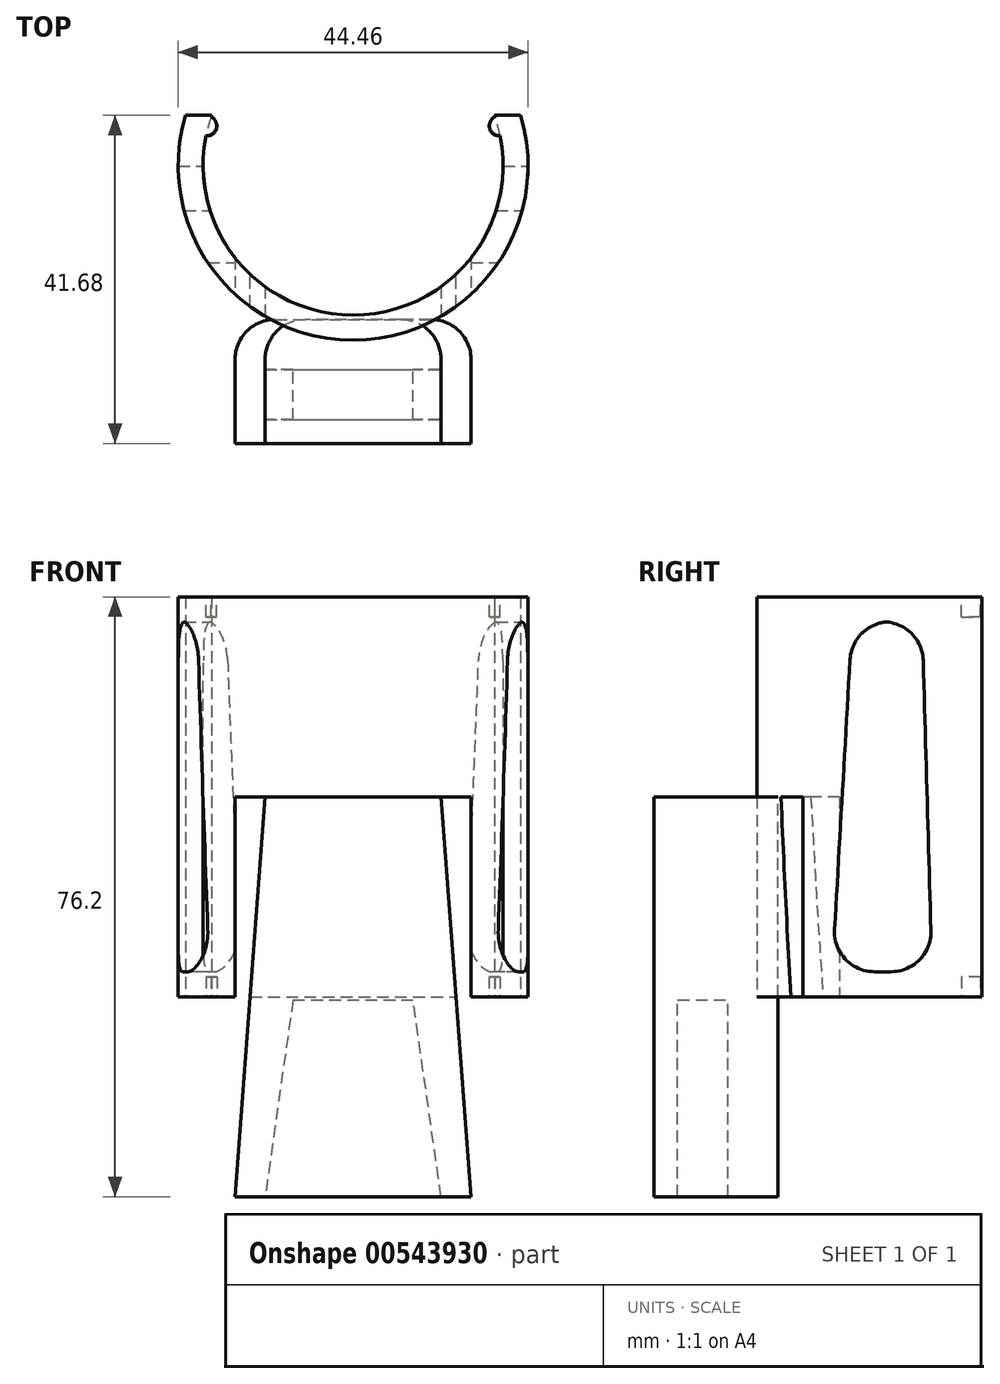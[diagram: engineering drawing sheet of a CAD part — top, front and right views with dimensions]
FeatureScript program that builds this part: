
annotation { "Feature Type Name" : "Feature", "Feature Type Description" : "" }
export const myFeature = defineFeature(function(context is Context, id is Id, definition is map)
    precondition{}
    {
        {
            var Q0;
            Q0=qCreatedBy(makeId("Top.planeOp"),FACE);
            var sketch = newSketch(context, id + "F0", { "sketchPlane" : qUnion([Q0])});
            skArc(sketch, "E0", {"start": v(-17.96, 6.35) * mm, "mid": v(0, -19.05) * mm, "end": v(17.96, 6.35) * mm});
            skArc(sketch, "E1.0", {"start": v(-21.3, 6.35) * mm, "mid": v(0, -22.23) * mm, "end": v(21.3, 6.35) * mm});
            skLineSegment(sketch, "E2", {"start": v(21.3, 6.35) * mm, "end": v(17.96, 6.35) * mm});
            skLineSegment(sketch, "E3.trimOffspring", {"start": v(-17.96, 6.35) * mm, "end": v(-21.3, 6.35) * mm});
            skSolve(sketch);
        }
        {
            var Q0;
            Q0=qSketchRegion(id+"F0",true);
            extrude(context, id + "F1", {"entities" : qUnion([Q0]), "depth" : 50.8 * mm});
        }
        {
            var Q0;
            Q0=qCreatedBy(makeId("Right.planeOp"),FACE);
            var sketch = newSketch(context, id + "F2", { "sketchPlane" : qUnion([Q0])});
            skLineSegment(sketch, "E4", {"start": v(-10.16, 47.63) * mm, "end": v(-1.27, 47.63) * mm});
            skLineSegment(sketch, "E5", {"start": v(-1.27, 47.63) * mm, "end": v(0, 3.18) * mm});
            skLineSegment(sketch, "E6", {"start": v(0, 3.18) * mm, "end": v(-12.7, 3.17) * mm});
            skLineSegment(sketch, "E7", {"start": v(-12.7, 3.18) * mm, "end": v(-10.16, 47.62) * mm});
            skSolve(sketch);
        }
        {
            var Q0;
            Q0=qSketchRegion(id+"F2",true);
            extrude(context, id + "F3", {"entities" : qUnion([Q0]), "operationType" : NewBodyOperationType.REMOVE, "endBound" : BoundingType.SYMMETRIC, "depth" : 78.74 * mm});
        }
        {
            var Q0;
            Q0=makeQuery(id+"F3.boolean.opBoolean","COPY",EDGE,{"disambiguationData":[OD(1.0)],"derivedFrom":makeQuery(id+"F3.opExtrude","SWEPT_EDGE",EDGE,{"disambiguationData":[OSD([sQuery(id+"F2.wireOp",EDGE,"E4"),sQuery(id+"F2.wireOp",EDGE,"E7")])]})});
            var Q1;
            Q1=makeQuery(id+"F3.boolean.opBoolean","COPY",EDGE,{"disambiguationData":[OD(1.0)],"derivedFrom":makeQuery(id+"F3.opExtrude","SWEPT_EDGE",EDGE,{"disambiguationData":[OSD([sQuery(id+"F2.wireOp",EDGE,"E4"),sQuery(id+"F2.wireOp",EDGE,"E5")])]})});
            var Q2;
            Q2=makeQuery(id+"F3.boolean.opBoolean","COPY",EDGE,{"disambiguationData":[OD(1.0)],"derivedFrom":makeQuery(id+"F3.opExtrude","SWEPT_EDGE",EDGE,{"disambiguationData":[OSD([sQuery(id+"F2.wireOp",EDGE,"E5"),sQuery(id+"F2.wireOp",EDGE,"E6")])]})});
            var Q3;
            Q3=makeQuery(id+"F3.boolean.opBoolean","COPY",EDGE,{"disambiguationData":[OD(1.0)],"derivedFrom":makeQuery(id+"F3.opExtrude","SWEPT_EDGE",EDGE,{"disambiguationData":[OSD([sQuery(id+"F2.wireOp",EDGE,"E6"),sQuery(id+"F2.wireOp",EDGE,"E7")])]})});
            var Q4;
            Q4=makeQuery(id+"F3.boolean.opBoolean","COPY",EDGE,{"disambiguationData":[OD(0.0)],"derivedFrom":makeQuery(id+"F3.opExtrude","SWEPT_EDGE",EDGE,{"disambiguationData":[OSD([sQuery(id+"F2.wireOp",EDGE,"E6"),sQuery(id+"F2.wireOp",EDGE,"E7")])]})});
            var Q5;
            Q5=makeQuery(id+"F3.boolean.opBoolean","COPY",EDGE,{"disambiguationData":[OD(0.0)],"derivedFrom":makeQuery(id+"F3.opExtrude","SWEPT_EDGE",EDGE,{"disambiguationData":[OSD([sQuery(id+"F2.wireOp",EDGE,"E5"),sQuery(id+"F2.wireOp",EDGE,"E6")])]})});
            var Q6;
            Q6=makeQuery(id+"F3.boolean.opBoolean","COPY",EDGE,{"disambiguationData":[OD(0.0)],"derivedFrom":makeQuery(id+"F3.opExtrude","SWEPT_EDGE",EDGE,{"disambiguationData":[OSD([sQuery(id+"F2.wireOp",EDGE,"E4"),sQuery(id+"F2.wireOp",EDGE,"E7")])]})});
            var Q7;
            Q7=makeQuery(id+"F3.boolean.opBoolean","COPY",EDGE,{"disambiguationData":[OD(0.0)],"derivedFrom":makeQuery(id+"F3.opExtrude","SWEPT_EDGE",EDGE,{"disambiguationData":[OSD([sQuery(id+"F2.wireOp",EDGE,"E4"),sQuery(id+"F2.wireOp",EDGE,"E5")])]})});
            fillet(context, id + "F4", {"entities" : qUnion([Q0, Q1, Q2, Q3, Q4, Q5, Q6, Q7]), "radius" : 5.08 * mm, "tangentPropagation" : true, "allowEdgeOverflow" : false});
        }
        {
            var Q0;
            Q0=makeQuery(id+"F1.opExtrude","CAP_EDGE",EDGE,{"disambiguationData":[OSD([sQuery(id+"F0.wireOp",EDGE,"E1.0")])],"isStart":false});
            cPoint(context, id + "F5", {"entities" : qUnion([Q0]), "parameter" : 0.5});
        }
        {
            var Q0;
            Q0=qCreatedBy(makeId("Front.planeOp"),FACE);
            var Q1;
            Q1=qCreatedBy(id+"F5",VERTEX);
            cPlane(context, id + "F6", {"entities" : qUnion([Q0, Q1]), "cplaneType" : CPlaneType.PLANE_POINT, "offset" : 25.4 * mm, "width" : 152.4 * mm, "height" : 152.4 * mm});
        }
        {
            var Q0;
            Q0=qCreatedBy(id+"F6.planeOp",FACE);
            var sketch = newSketch(context, id + "F7", { "sketchPlane" : qUnion([Q0])});
            skLineSegment(sketch, "E8", {"start": v(14.99, 25.4) * mm, "end": v(14.99, -25.4) * mm});
            skLineSegment(sketch, "E9.MirrorCS", {"start": v(-14.99, 25.4) * mm, "end": v(-14.99, -25.4) * mm});
            skLineSegment(sketch, "E10", {"start": v(-14.99, -25.4) * mm, "end": v(14.99, -25.4) * mm});
            skLineSegment(sketch, "E11", {"start": v(14.99, 25.4) * mm, "end": v(-14.99, 25.4) * mm});
            skLineSegment(sketch, "E12", {"start": v(0, -1.18) * mm, "end": v(0, 25.4) * mm});
            skSolve(sketch);
        }
        {
            var Q0;
            Q0=qSketchRegion(id+"F7",true);
            extrude(context, id + "F8", {"entities" : qUnion([Q0]), "operationType" : NewBodyOperationType.ADD, "depth" : 15.75 * mm, "offsetDistance" : 25.4 * mm});
        }
        {
            var Q0;
            Q0=makeQuery(id+"F8.opExtrude","CAP_FACE",FACE,{"disambiguationData":[OSD([sQuery(id+"F7.wireOp",EDGE,"E8"),sQuery(id+"F7.wireOp",EDGE,"E9.MirrorCS"),sQuery(id+"F7.wireOp",EDGE,"E10"),sQuery(id+"F7.wireOp",EDGE,"E11")])],"isStart":false});
            var sketch = newSketch(context, id + "F9", { "sketchPlane" : qUnion([Q0])});
            skLineSegment(sketch, "E13", {"start": v(-11.18, 25.4) * mm, "end": v(11.18, 25.4) * mm});
            skLineSegment(sketch, "E14", {"start": v(14.99, -25.4) * mm, "end": v(11.18, 25.4) * mm});
            skLineSegment(sketch, "E15.MirrorCS", {"start": v(-14.99, -25.4) * mm, "end": v(-11.18, 25.4) * mm});
            skPoint(sketch, "E16.orphan", {"position": v(14.99, 25.4) * mm});
            skPoint(sketch, "E17.orphan", {"position": v(-14.99, 25.4) * mm});
            skPoint(sketch, "E18.end.orphan", {"position": v(0, 25.4) * mm});
            skLineSegment(sketch, "E19", {"start": v(-11.18, 25.4) * mm, "end": v(-14.99, 25.4) * mm});
            skLineSegment(sketch, "E20", {"start": v(11.18, 25.4) * mm, "end": v(14.99, 25.4) * mm});
            skSolve(sketch);
        }
        {
            var Q0;
            Q0=makeQuery(id+"F9.imprint","IMPRINT",FACE,{"disambiguationData":[TD([[makeQuery(id+"F9.imprint","IMPRINT",EDGE,{"derivedFrom":sQuery(id+"F9.wireOp",EDGE,"E15.MirrorCS")}),1.0]])]});
            var Q1;
            Q1=makeQuery(id+"F9.imprint","IMPRINT",FACE,{"disambiguationData":[TD([[makeQuery(id+"F9.imprint","IMPRINT",EDGE,{"derivedFrom":sQuery(id+"F9.wireOp",EDGE,"E14")}),-1.0]])]});
            extrude(context, id + "F10", {"entities" : qUnion([Q0, Q1]), "operationType" : NewBodyOperationType.REMOVE, "oppositeDirection" : true, "depth" : 127 * mm, "offsetDistance" : 25.4 * mm});
        }
        {
            var Q0;
            Q0=makeQuery(id+"F1.opExtrude","SWEPT_BODY",BODY,{"disambiguationData":[OSD([sQuery(id+"F0.wireOp",EDGE,"E0"),sQuery(id+"F0.wireOp",EDGE,"E1.0"),sQuery(id+"F0.wireOp",EDGE,"E2"),sQuery(id+"F0.wireOp",EDGE,"E3.trimOffspring")])]});
            transform(context, id + "F11", {"entities" : qUnion([Q0]), "transformType" : TransformType.TRANSLATION_3D, "dx" : 0 * mm, "dy" : -2.64 * mm, "dz" : 0 * mm, "makeCopy" : false});
        }
        {
            var Q0;
            Q0=qCreatedBy(makeId("Top.planeOp"),FACE);
            var sketch = newSketch(context, id + "F12", { "sketchPlane" : qUnion([Q0])});
            skCircle(sketch, "E21", {"center": v(18.56, 2.35) * mm, "radius": 1.27 * mm});
            skCircle(sketch, "E22.MirrorC", {"center": v(-18.56, 2.35) * mm, "radius": 1.27 * mm});
            skSolve(sketch);
        }
        {
            var Q0;
            Q0=qSketchRegion(id+"F12",true);
            extrude(context, id + "F13", {"entities" : qUnion([Q0]), "operationType" : NewBodyOperationType.ADD, "depth" : 2.54 * mm, "offsetDistance" : 25.4 * mm});
        }
        {
            var Q0;
            Q0=qCreatedBy(makeId("Top.planeOp"),FACE);
            cPlane(context, id + "F14", {"entities" : qUnion([Q0]), "cplaneType" : CPlaneType.OFFSET, "offset" : 50.8 * mm, "width" : 152.4 * mm, "height" : 152.4 * mm});
        }
        {
            var Q0;
            Q0=qCreatedBy(id+"F14.planeOp",FACE);
            var sketch = newSketch(context, id + "F15", { "sketchPlane" : qUnion([Q0])});
            skCircle(sketch, "E23", {"center": v(-18.6, 2.37) * mm, "radius": 1.27 * mm});
            skCircle(sketch, "E24.MirrorC", {"center": v(18.6, 2.37) * mm, "radius": 1.27 * mm});
            skSolve(sketch);
        }
        {
            var Q0;
            Q0=qSketchRegion(id+"F15",true);
            extrude(context, id + "F16", {"entities" : qUnion([Q0]), "operationType" : NewBodyOperationType.ADD, "oppositeDirection" : true, "depth" : 2.54 * mm, "offsetDistance" : 25.4 * mm});
        }
        {
            var Q0;
            Q0=qCreatedBy(id+"F6.planeOp",FACE);
            cPlane(context, id + "F17", {"entities" : qUnion([Q0]), "cplaneType" : CPlaneType.OFFSET, "offset" : 9.55 * mm, "width" : 152.4 * mm, "height" : 152.4 * mm});
        }
        {
            var Q0;
            Q0=qCreatedBy(id+"F17.planeOp",FACE);
            var sketch = newSketch(context, id + "F18", { "sketchPlane" : qUnion([Q0])});
            skLineSegment(sketch, "E25.0", {"start": v(11.18, -25.4) * mm, "end": v(7.63, -0.43) * mm});
            skLineSegment(sketch, "E26", {"start": v(-11.18, -25.4) * mm, "end": v(11.18, -25.4) * mm});
            skLineSegment(sketch, "E27", {"start": v(-7.63, -0.43) * mm, "end": v(7.63, -0.43) * mm});
            skLineSegment(sketch, "E28", {"start": v(-7.63, -0.43) * mm, "end": v(-11.18, -25.4) * mm});
            skSolve(sketch);
        }
        {
            var Q0;
            Q0 = qSketchRegion(id + "F18", true);
            extrude(context, id + "F19", {"entities" : qUnion([Q0]), "operationType" : NewBodyOperationType.REMOVE, "endBound" : BoundingType.SYMMETRIC, "depth" : 6.4 * mm, "offsetDistance" : 25.4 * mm});
        }
        {
            var Q0;
            Q0=makeQuery(id+"F10.boolean.opBoolean","INTERSECT",EDGE,{"derivedFrom":[makeQuery(id+"F8.opExtrude","CAP_FACE",FACE,{"disambiguationData":[OSD([sQuery(id+"F7.wireOp",EDGE,"E8"),sQuery(id+"F7.wireOp",EDGE,"E9.MirrorCS"),sQuery(id+"F7.wireOp",EDGE,"E10"),sQuery(id+"F7.wireOp",EDGE,"E11")])],"isStart":true}),makeQuery(id+"F10.opExtrude","SWEPT_FACE",FACE,{"disambiguationData":[OSD([sQuery(id+"F9.wireOp",EDGE,"E14")])]})]});
            var Q1;
            Q1=makeQuery(id+"F10.boolean.opBoolean","COPY",EDGE,{"derivedFrom":makeQuery(id+"F10.opExtrude","CAP_EDGE",EDGE,{"disambiguationData":[OSD([sQuery(id+"F9.wireOp",EDGE,"E14")])],"isStart":true})});
            var Q2;
            Q2=makeQuery(id+"F10.boolean.opBoolean","INTERSECT",EDGE,{"derivedFrom":[makeQuery(id+"F8.opExtrude","CAP_FACE",FACE,{"disambiguationData":[OSD([sQuery(id+"F7.wireOp",EDGE,"E8"),sQuery(id+"F7.wireOp",EDGE,"E9.MirrorCS"),sQuery(id+"F7.wireOp",EDGE,"E10"),sQuery(id+"F7.wireOp",EDGE,"E11")])],"isStart":true}),makeQuery(id+"F10.opExtrude","SWEPT_FACE",FACE,{"disambiguationData":[OSD([sQuery(id+"F9.wireOp",EDGE,"E15.MirrorCS")])]})]});
            var Q3;
            Q3=makeQuery(id+"F10.boolean.opBoolean","COPY",EDGE,{"derivedFrom":makeQuery(id+"F10.opExtrude","CAP_EDGE",EDGE,{"disambiguationData":[OSD([sQuery(id+"F9.wireOp",EDGE,"E15.MirrorCS")])],"isStart":true})});
            fillet(context, id + "F20", {"entities" : qUnion([Q0, Q1, Q2, Q3]), "radius" : 5.08 * mm, "tangentPropagation" : true, "allowEdgeOverflow" : false});
        }
    });
